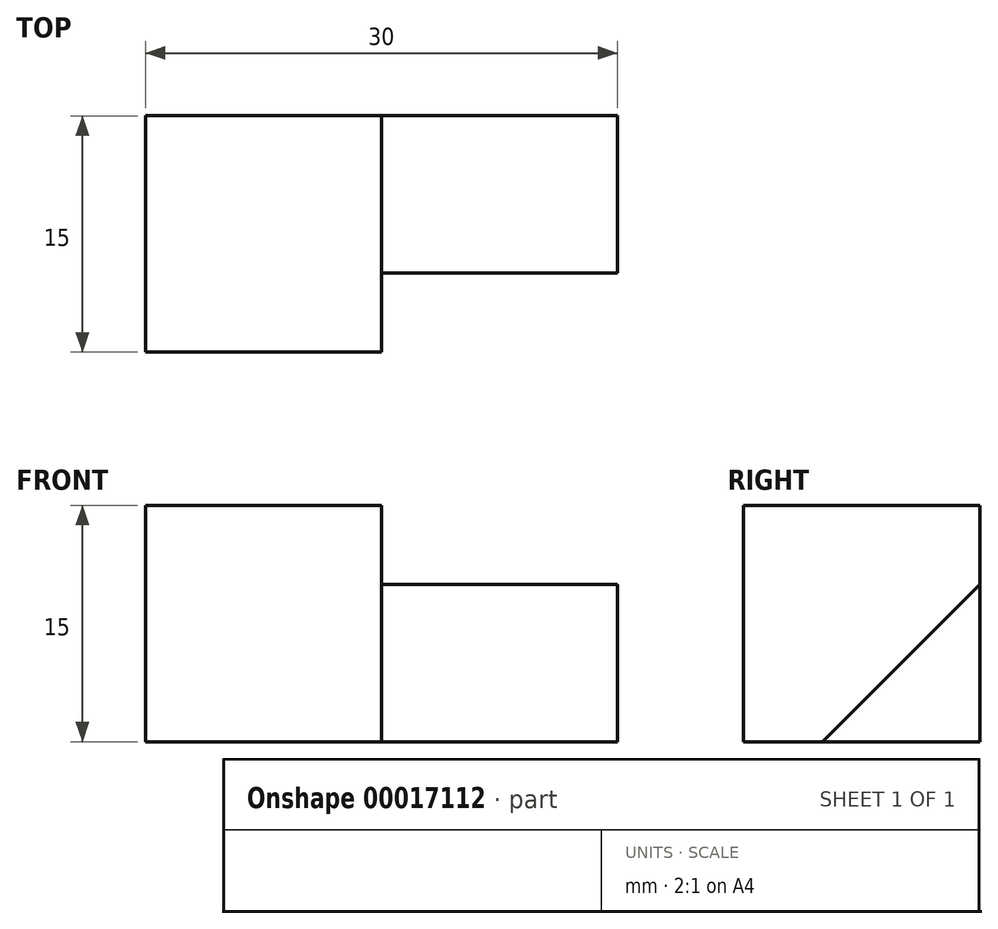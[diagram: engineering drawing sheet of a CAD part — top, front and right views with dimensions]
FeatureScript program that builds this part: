
annotation { "Feature Type Name" : "Feature", "Feature Type Description" : "" }
export const myFeature = defineFeature(function(context is Context, id is Id, definition is map)
    precondition{}
    {
        {
            var Q0;
            Q0=qCreatedBy(makeId("Right.planeOp"),FACE);
            var sketch = newSketch(context, id + "F0", { "sketchPlane" : qUnion([Q0])});
            skLineSegment(sketch, "E0.bottom", {"start": v(-29.2, 26.45) * mm, "end": v(-14.2, 26.45) * mm});
            skLineSegment(sketch, "E0.left", {"start": v(-29.2, 26.45) * mm, "end": v(-29.2, 11.45) * mm});
            skLineSegment(sketch, "E1", {"start": v(-29.2, 11.45) * mm, "end": v(-24.2, 11.45) * mm});
            skLineSegment(sketch, "E2", {"start": v(-24.2, 11.45) * mm, "end": v(-14.2, 21.45) * mm});
            skLineSegment(sketch, "E3", {"start": v(-14.2, 21.45) * mm, "end": v(-14.2, 26.45) * mm});
            skLineSegment(sketch, "E4", {"start": v(-14.2, 21.45) * mm, "end": v(-14.2, 11.45) * mm});
            skLineSegment(sketch, "E5", {"start": v(-24.2, 11.45) * mm, "end": v(-14.2, 11.45) * mm});
            skSolve(sketch);
        }
        {
            var Q0;
            Q0=makeQuery(id+"F0.imprint","IMPRINT",FACE,{"disambiguationData":[TD([[makeQuery(id+"F0.imprint","IMPRINT",EDGE,{"derivedFrom":sQuery(id+"F0.wireOp",EDGE,"E2")}),-1.0]])]});
            extrude(context, id + "F1", {"entities" : qUnion([Q0]), "depth" : 30 * mm});
        }
        {
            var Q0;
            Q0=makeQuery(id+"F0.imprint","IMPRINT",FACE,{"disambiguationData":[TD([[makeQuery(id+"F0.imprint","IMPRINT",EDGE,{"derivedFrom":sQuery(id+"F0.wireOp",EDGE,"E0.bottom")}),-1.0]])]});
            extrude(context, id + "F2", {"entities" : qUnion([Q0]), "operationType" : NewBodyOperationType.ADD, "depth" : 15 * mm});
        }
    });
